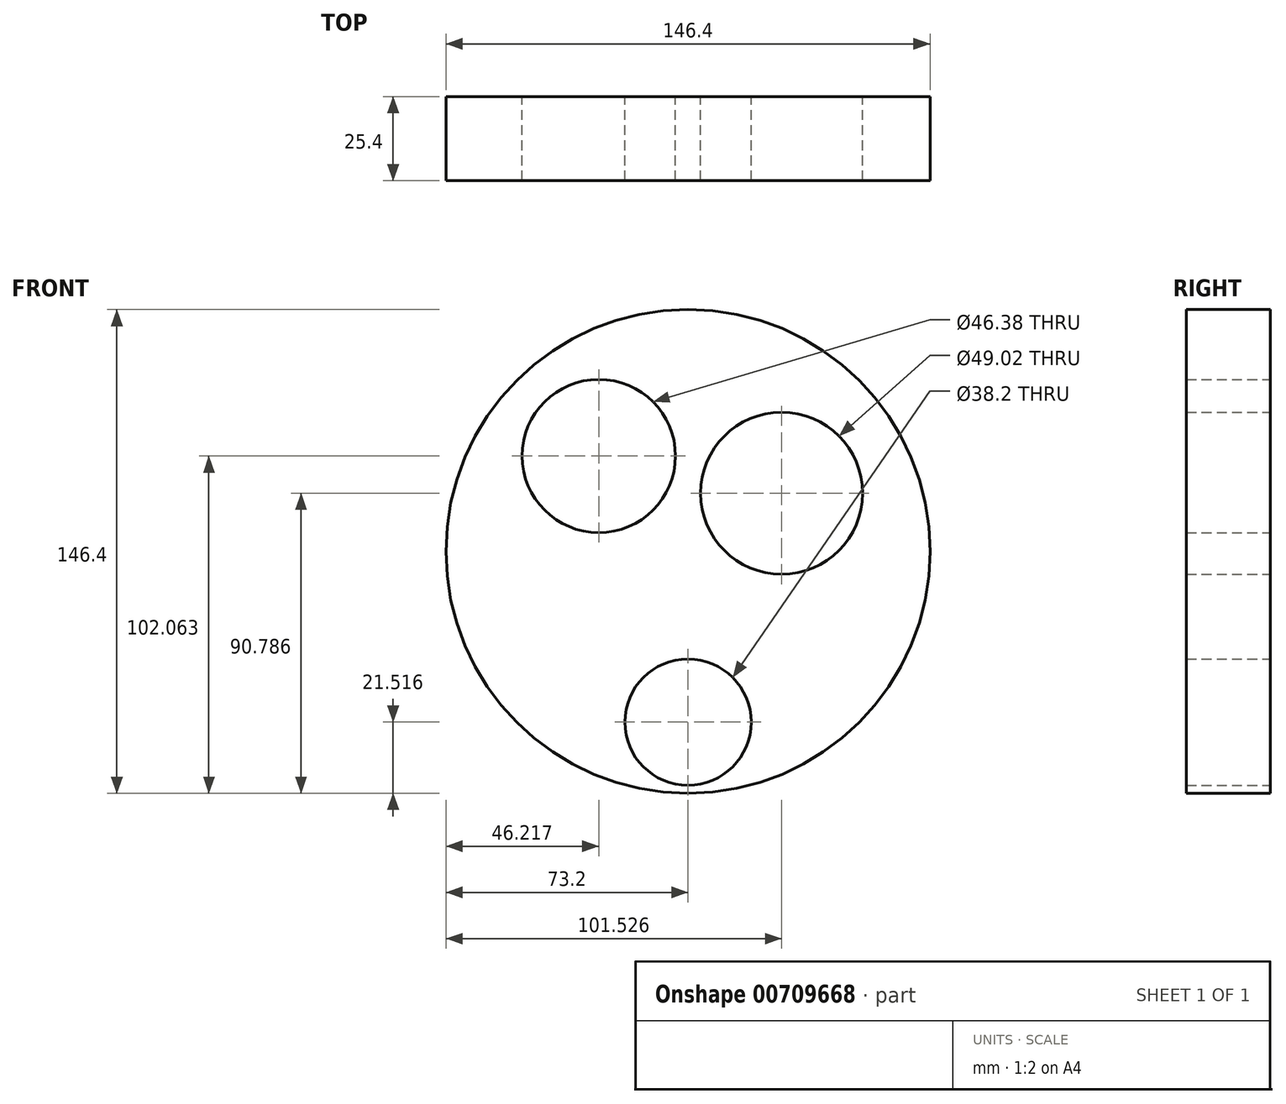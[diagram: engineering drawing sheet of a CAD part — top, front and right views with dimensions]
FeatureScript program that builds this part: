
annotation { "Feature Type Name" : "Feature", "Feature Type Description" : "" }
export const myFeature = defineFeature(function(context is Context, id is Id, definition is map)
    precondition{}
    {
        {
            var Q0;
            Q0=qCreatedBy(makeId("Front.planeOp"),FACE);
            var sketch = newSketch(context, id + "F0", { "sketchPlane" : qUnion([Q0])});
            skCircle(sketch, "E0", {"center": v(0, 0) * mm, "radius": 73.2 * mm});
            skCircle(sketch, "E1", {"center": v(-26.98, 28.86) * mm, "radius": 23.19 * mm});
            skCircle(sketch, "E2", {"center": v(28.33, 17.59) * mm, "radius": 24.5 * mm});
            skCircle(sketch, "E3", {"center": v(0, -51.68) * mm, "radius": 19.1 * mm});
            skSolve(sketch);
        }
        {
            var Q0;
            Q0=makeQuery(id+"F0.imprint","IMPRINT",FACE,{"disambiguationData":[TD([[makeQuery(id+"F0.imprint","IMPRINT",EDGE,{"derivedFrom":sQuery(id+"F0.wireOp",EDGE,"E0")}),1.0]])]});
            extrude(context, id + "F1", {"entities" : qUnion([Q0]), "depth" : 25.4 * mm, "offsetDistance" : 25.4 * mm});
        }
    });
